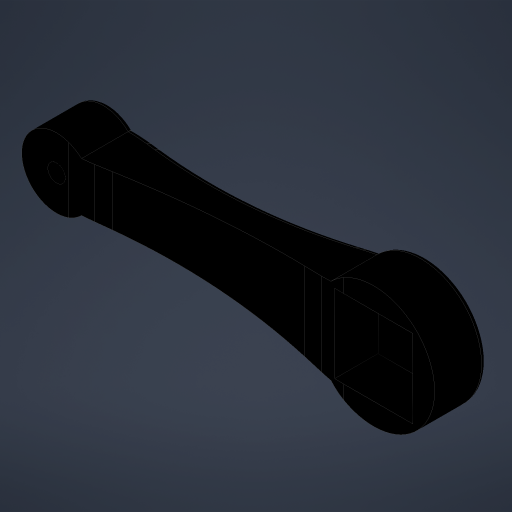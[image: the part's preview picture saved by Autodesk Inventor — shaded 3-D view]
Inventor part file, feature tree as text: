
AUTODESK INVENTOR PART (.ipt)
format: ipt  version: 2023 (Build 270158000, 158)  size: 433,152 bytes
history: native  units: mm
features: extrude x6, fillet x6, sketch x6, chamfer x4
ambient origin geometry x8: Origin, YZ Plane, XZ Plane, XY Plane, X Axis, Y Axis, Z Axis, Center Point
bodies: Solid1 (feature_tree)
feature tree (22):
  extrude  "Extrusion1"  Depth=70.0mm
  extrude  "Extrusion2"  Depth=10.0mm TaperAngle=0.0deg
  chamfer  "Chamfer1"  Distance=10.0mm Angle=45.0deg
  chamfer  "Chamfer2"  Distance=10.0mm Angle=45.0deg
  fillet  "Fillet1"  Radius=400.0mm
  fillet  "Fillet2"  Radius=100.0mm
  fillet  "Fillet3"  Radius=3.0mm
  extrude  "Extrusion3"  Depth=10.0mm
  extrude  "Extrusion4"  Depth=22.5mm
  sketch  "Sketch5"  dims[d34=22.5mm]
  chamfer  "Chamfer5"  Distance=45.0mm
  chamfer  "Chamfer6"  Distance=10.0mm Angle=45.0deg
  fillet  "Fillet7"  Radius=9.9mm
  fillet  "Fillet8"  Radius=400.0mm
  extrude  "Extrusion5"  Depth=100.0mm
  extrude  "Extrusion6"  Depth=25.0mm TaperAngle=0.0deg
  fillet  "Fillet9"  Radius=50.0mm
  sketch  "Sketch1"  dims[d0=40.0mm d2=70.0mm]
  sketch  "Sketch2"  dims[d6=30.0mm d7=0.0mm d8=10.0mm d9=0.0mm d10=10.0mm d11=70.0mm d12=45.0deg d13=10.0mm d14=68.18mm d15=45.0deg d16=400.0mm d17=100.0mm d18=3.0mm]
  sketch  "Sketch3"  dims[d19=10.0mm d20=0.0mm d30=10.0mm]
  sketch  "Sketch4"  dims[d31=30.0mm d32=0.0mm d33=22.5mm]
  sketch  "Sketch6"  dims[d35=45.0mm d36=45.0mm d39=10.0mm d40=71.0mm d41=45.0deg d42=9.9mm d43=72.459481mm d44=45.0deg d45=400.0mm d46=100.0mm d47=25.0mm d48=0.0mm d49=50.0mm d50=25.0mm d51=2.0mm d52=0.0mm d53=1.0mm]
